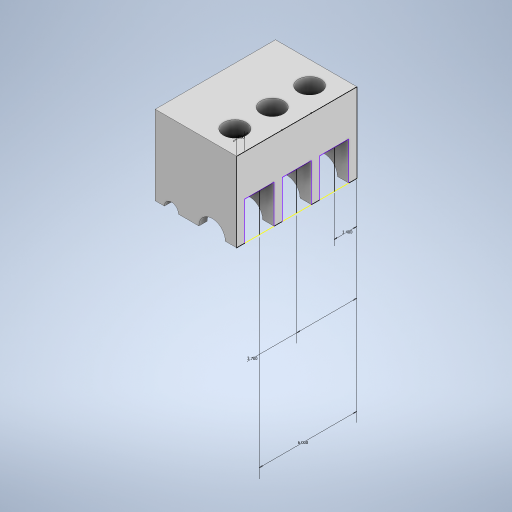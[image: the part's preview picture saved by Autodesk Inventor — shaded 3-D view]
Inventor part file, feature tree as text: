
AUTODESK INVENTOR PART (.ipt)
format: ipt  version: 2023 (Build 270158000, 158)  size: 342,528 bytes
history: native  units: in
note: dims shown in document units (in); Inventor stores cm internally (conversion verified against a paired STEP export)
features: extrude x4, sketch x3
ambient origin geometry x8: Origin, YZ Plane, XZ Plane, XY Plane, X Axis, Y Axis, Z Axis, Center Point
bodies: Solid1 (feature_tree)
feature tree (7):
  extrude  "Extrusion1"  Depth=4.878in
  sketch  "Sketch2"  dims[d2=1.625in d3=7.4in d4=0.0in]
  extrude  "Extrusion2"  Depth=7.4in TaperAngle=0.0deg
  extrude  "Extrusion3"  Depth=1.5in
  extrude  "Extrusion4"  Depth=1.5in
  sketch  "Sketch1"  dims[d0=5.0in d1=4.878in]
  sketch  "Sketch4"  dims[d6=1.4in d7=1.5in d10=1.4in d11=1.5in d13=2.3in d14=1.5in d15=1.4in d16=3.7in d17=6.0in d18=0.5in d20=2.528in d21=7.4in d22=0.0in d23=7.4in d24=0.0in d25=1.5in d26=0.866in d27=1.5in d28=0.0in d29=1.4in d30=0.0in d31=0.0in d32=0.0in]
